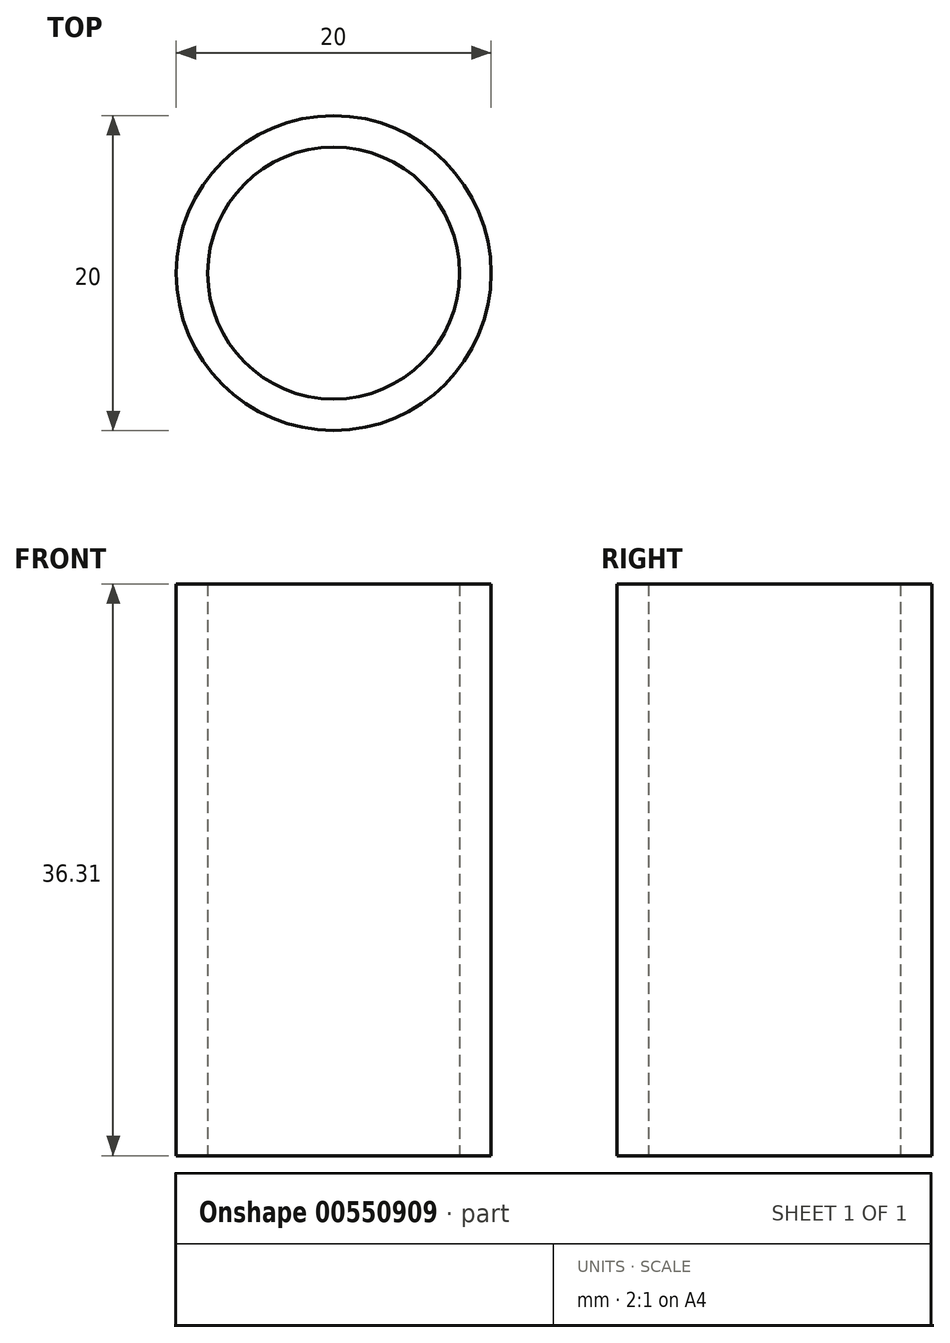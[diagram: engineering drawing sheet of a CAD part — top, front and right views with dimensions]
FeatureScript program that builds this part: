
annotation { "Feature Type Name" : "Feature", "Feature Type Description" : "" }
export const myFeature = defineFeature(function(context is Context, id is Id, definition is map)
    precondition{}
    {
        {
            var Q0;
            Q0=qCreatedBy(makeId("Top.planeOp"),FACE);
            var sketch = newSketch(context, id + "F0", { "sketchPlane" : qUnion([Q0])});
            skCircle(sketch, "E0", {"center": v(0, 0) * mm, "radius": 10 * mm});
            skSolve(sketch);
        }
        {
            var Q0;
            Q0 = qSketchRegion(id + "F0", true);
            extrude(context, id + "F1", {"entities" : qUnion([Q0]), "depth" : 36.3 * mm, "offsetDistance" : 25 * mm});
        }
        {
            var Q0;
            Q0=sQuery(id+"F0.wireOp",VERTEX,"E0.center");
            var Q1;
            Q1=makeQuery(id+"F1.opExtrude","SWEPT_BODY",BODY,{"disambiguationData":[OSD([sQuery(id+"F0.wireOp",EDGE,"E0")])]});
            hole(context, id + "F2", {"style" : HoleStyle.SIMPLE, "endStyle" : HoleEndStyle.THROUGH, "oppositeDirection" : true, "holeDiameter" : 16 * mm, "majorDiameter" : 5 * mm, "isTappedThrough" : true, "tappedDepth" : 12 * mm, "tapClearance" : 3, "locations" : qUnion([Q0]), "scope" : qUnion([Q1])});
        }
    });
